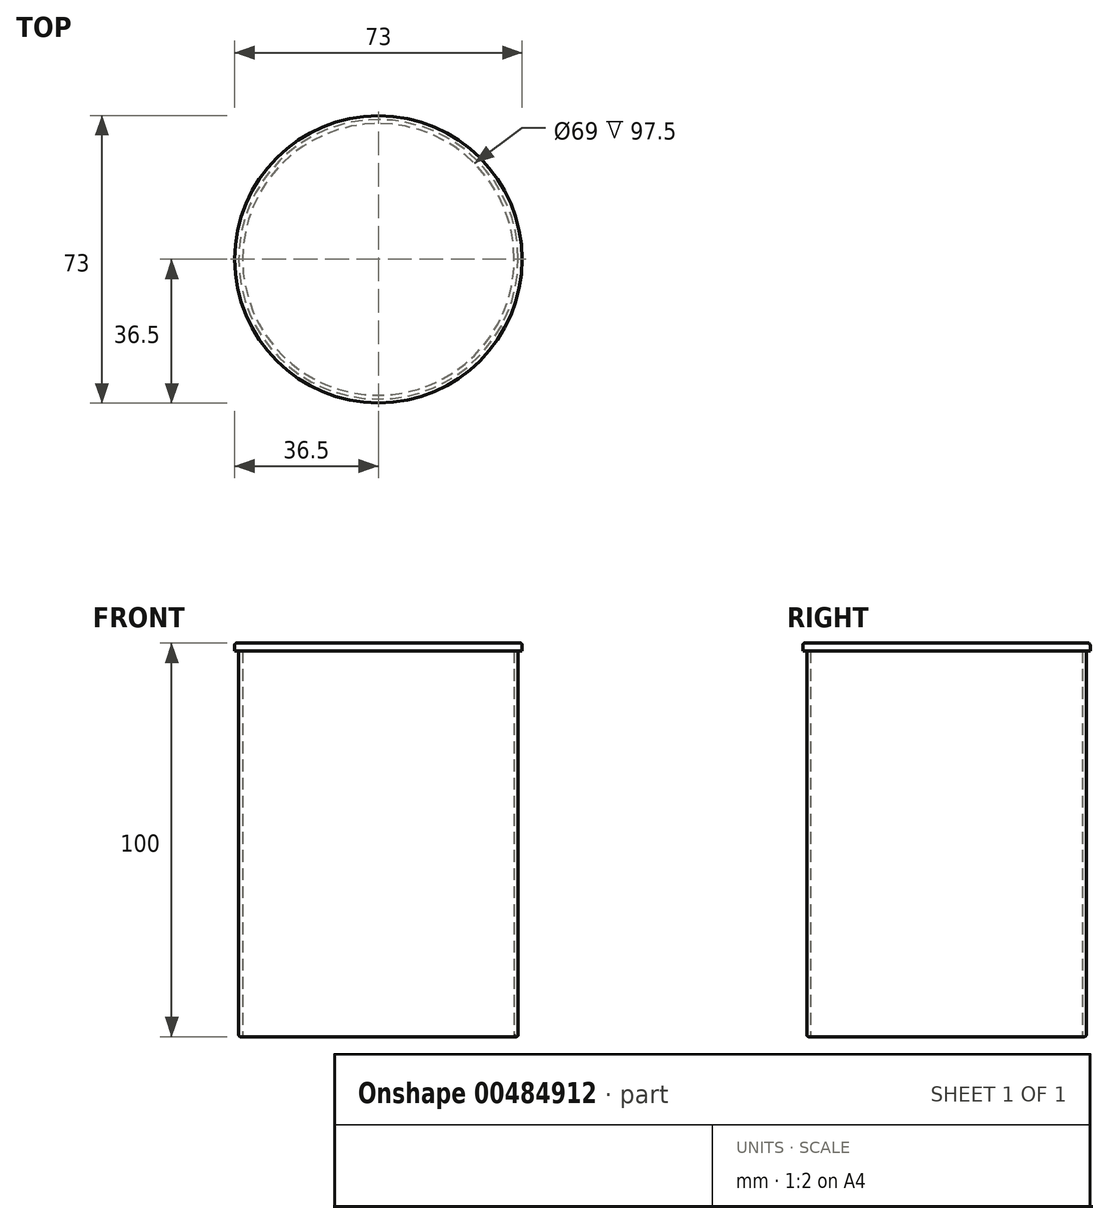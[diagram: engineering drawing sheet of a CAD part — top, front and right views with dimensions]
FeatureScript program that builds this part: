
annotation { "Feature Type Name" : "Feature", "Feature Type Description" : "" }
export const myFeature = defineFeature(function(context is Context, id is Id, definition is map)
    precondition{}
    {
        {
            var Q0;
            Q0=qCreatedBy(makeId("Top.planeOp"),FACE);
            var sketch = newSketch(context, id + "F0", { "sketchPlane" : qUnion([Q0])});
            skCircle(sketch, "E0", {"center": v(0, 0) * mm, "radius": 34.5 * mm});
            skCircle(sketch, "E1.0", {"center": v(0, 0) * mm, "radius": 35.5 * mm});
            skSolve(sketch);
        }
        {
            var Q0;
            Q0=qSketchRegion(id+"F0",true);
            extrude(context, id + "F1", {"entities" : qUnion([Q0]), "depth" : 100 * mm});
        }
        {
            var Q0;
            Q0=makeQuery(id+"F1.opExtrude","CAP_FACE",FACE,{"disambiguationData":[OSD([sQuery(id+"F0.wireOp",EDGE,"E0"),sQuery(id+"F0.wireOp",EDGE,"E1.0")])],"isStart":false});
            var sketch = newSketch(context, id + "F2", { "sketchPlane" : qUnion([Q0])});
            skCircle(sketch, "E2", {"center": v(0, 0) * mm, "radius": 36.5 * mm});
            skSolve(sketch);
        }
        {
            var Q0;
            Q0=qSketchRegion(id+"F2",true);
            extrude(context, id + "F3", {"entities" : qUnion([Q0]), "operationType" : NewBodyOperationType.ADD, "oppositeDirection" : true, "depth" : 2 * mm});
        }
        {
            var Q0;
            Q0=makeQuery(id+"F1.opExtrude","CAP_FACE",FACE,{"disambiguationData":[OSD([sQuery(id+"F0.wireOp",EDGE,"E0"),sQuery(id+"F0.wireOp",EDGE,"E1.0")])],"isStart":true});
            var Q1;
            Q1=makeQuery(id+"F3.opExtrude","CAP_EDGE",EDGE,{"disambiguationData":[OSD([sQuery(id+"F2.wireOp",EDGE,"E2")])],"isStart":true});
            fillet(context, id + "F4", {"entities" : qUnion([Q0, Q1]), "radius" : .5 * mm, "tangentPropagation" : true, "allowEdgeOverflow" : false});
        }
    });
